# Revit family: d024e51d-fd6e-4257-bddc-13dd6d22a686
name_source: partatom
category: Furniture
revit_build: Autodesk Revit 2016 (Build: 20161004_0715(x64)
units: mm (PartAtom-declared; Revit-internal decimal feet)

## family parameters
Always vertical = Yes
Cut with Voids When Loaded = No
OmniClass Number = 23.40.20.00
OmniClass Title = General Furniture and Specialties
Room Calculation Point = No
Shared = No
Work Plane-Based = No

## types (1)
- Standard
    Depth = 23 11/16"
    Description = SUICIDE RESISTANT ATTENDA DESK
    Height = 29 1/4"
    Manufacturer = Behavioral Safety Products
    Manufacturer Fax = 706-705-1191
    Model = BF920
    Product Brochure URL = http://besafeprod.com
    Product Page URL = http://www.besafeprod.com
    Revit Object Download Link = http://library.smartbim.com
    Surface = Plastic - Behavioral Safety - High Pressure Laminate
    Type Image = <None>
    URL = http://besafeprod.com
    Unit = Plastic - Behavioral Safety - Polyurethane Foam
    Width = 35 9/16"

## geometry (parser evidence)
native form markers: Blend x4, Sweep x4
no freeform markers — native parametric forms only
